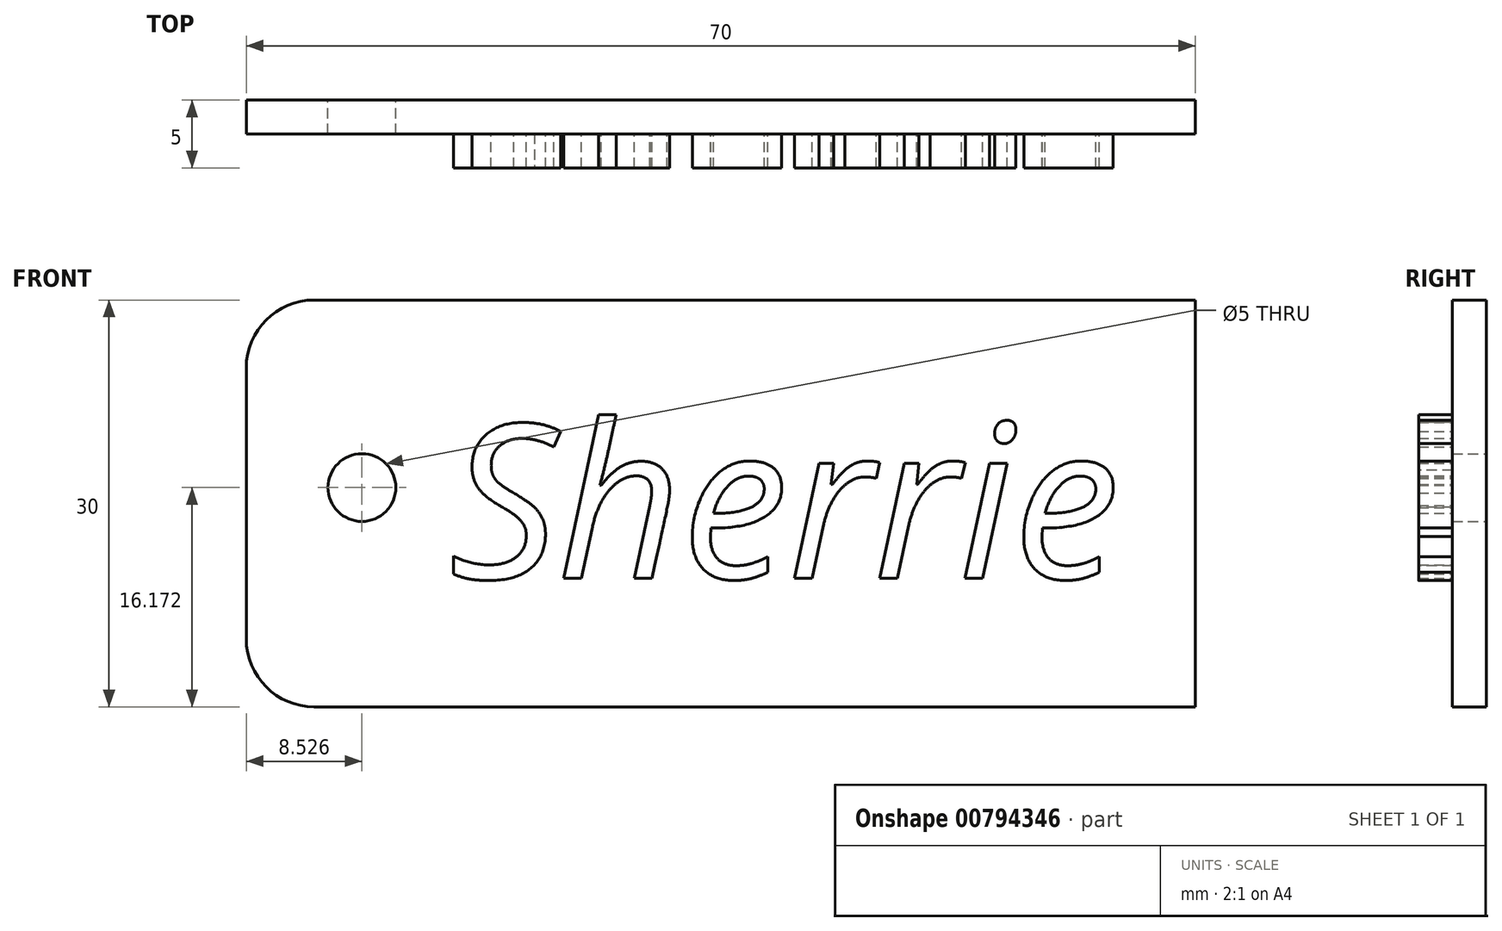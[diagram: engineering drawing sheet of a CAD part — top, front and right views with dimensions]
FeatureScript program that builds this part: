
annotation { "Feature Type Name" : "Feature", "Feature Type Description" : "" }
export const myFeature = defineFeature(function(context is Context, id is Id, definition is map)
    precondition{}
    {
        {
            var Q0;
            Q0=qCreatedBy(makeId("Front.planeOp"),FACE);
            var sketch = newSketch(context, id + "F0", { "sketchPlane" : qUnion([Q0])});
            skLineSegment(sketch, "E0.bottom", {"start": v(-26.88, 18.15) * mm, "end": v(43.12, 18.15) * mm});
            skLineSegment(sketch, "E0.top", {"start": v(-26.88, -11.85) * mm, "end": v(43.12, -11.85) * mm});
            skLineSegment(sketch, "E0.left", {"start": v(-26.88, 18.15) * mm, "end": v(-26.88, -11.85) * mm});
            skLineSegment(sketch, "E0.right", {"start": v(43.12, 18.15) * mm, "end": v(43.12, -11.85) * mm});
            skCircle(sketch, "E1", {"center": v(-18.35, 4.32) * mm, "radius": 2.5 * mm});
            skSolve(sketch);
        }
        {
            var Q0;
            Q0=makeQuery(id+"F0.imprint","IMPRINT",FACE,{"disambiguationData":[TD([[makeQuery(id+"F0.imprint","IMPRINT",EDGE,{"derivedFrom":sQuery(id+"F0.wireOp",EDGE,"E0.bottom")}),-1.0]])]});
            extrude(context, id + "F1", {"entities" : qUnion([Q0]), "depth" : 2.5 * mm, "offsetDistance" : 25 * mm});
        }
        {
            var Q0;
            Q0=makeQuery(id+"F1.opExtrude","CAP_FACE",FACE,{"disambiguationData":[OSD([sQuery(id+"F0.wireOp",EDGE,"E0.bottom"),sQuery(id+"F0.wireOp",EDGE,"E0.top"),sQuery(id+"F0.wireOp",EDGE,"E0.left"),sQuery(id+"F0.wireOp",EDGE,"E0.right"),sQuery(id+"F0.wireOp",EDGE,"E1")])],"isStart":false});
            var sketch = newSketch(context, id + "F2", { "sketchPlane" : qUnion([Q0])});
            skText(sketch, "E2", { "text": "Sherrie", "fontName": "OpenSans-Italic.ttf"});
            const initialGuessF2  = {"E2": [-0.0119, -0.00238, 1, 0, 0.01144]};
            skSetInitialGuess(sketch, initialGuessF2);
            skSolve(sketch);
        }
        {
            var Q0;
            Q0 = qSketchRegion(id + "F2", true);
            extrude(context, id + "F3", {"entities" : qUnion([Q0]), "operationType" : NewBodyOperationType.ADD, "depth" : 2.5 * mm, "offsetDistance" : 25 * mm});
        }
        {
            var Q0;
            Q0=makeQuery(id+"F1.opExtrude","SWEPT_EDGE",EDGE,{"disambiguationData":[OSD([sQuery(id+"F0.wireOp",EDGE,"E0.bottom"),sQuery(id+"F0.wireOp",EDGE,"E0.left")])]});
            fillet(context, id + "F4", {"entities" : qUnion([Q0]), "radius" : 5 * mm, "tangentPropagation" : true, "allowEdgeOverflow" : false});
        }
        {
            var Q0;
            Q0=makeQuery(id+"F1.opExtrude","SWEPT_EDGE",EDGE,{"disambiguationData":[OSD([sQuery(id+"F0.wireOp",EDGE,"E0.top"),sQuery(id+"F0.wireOp",EDGE,"E0.left")])]});
            fillet(context, id + "F5", {"entities" : qUnion([Q0]), "radius" : 5 * mm, "tangentPropagation" : true, "allowEdgeOverflow" : false});
        }
    });
